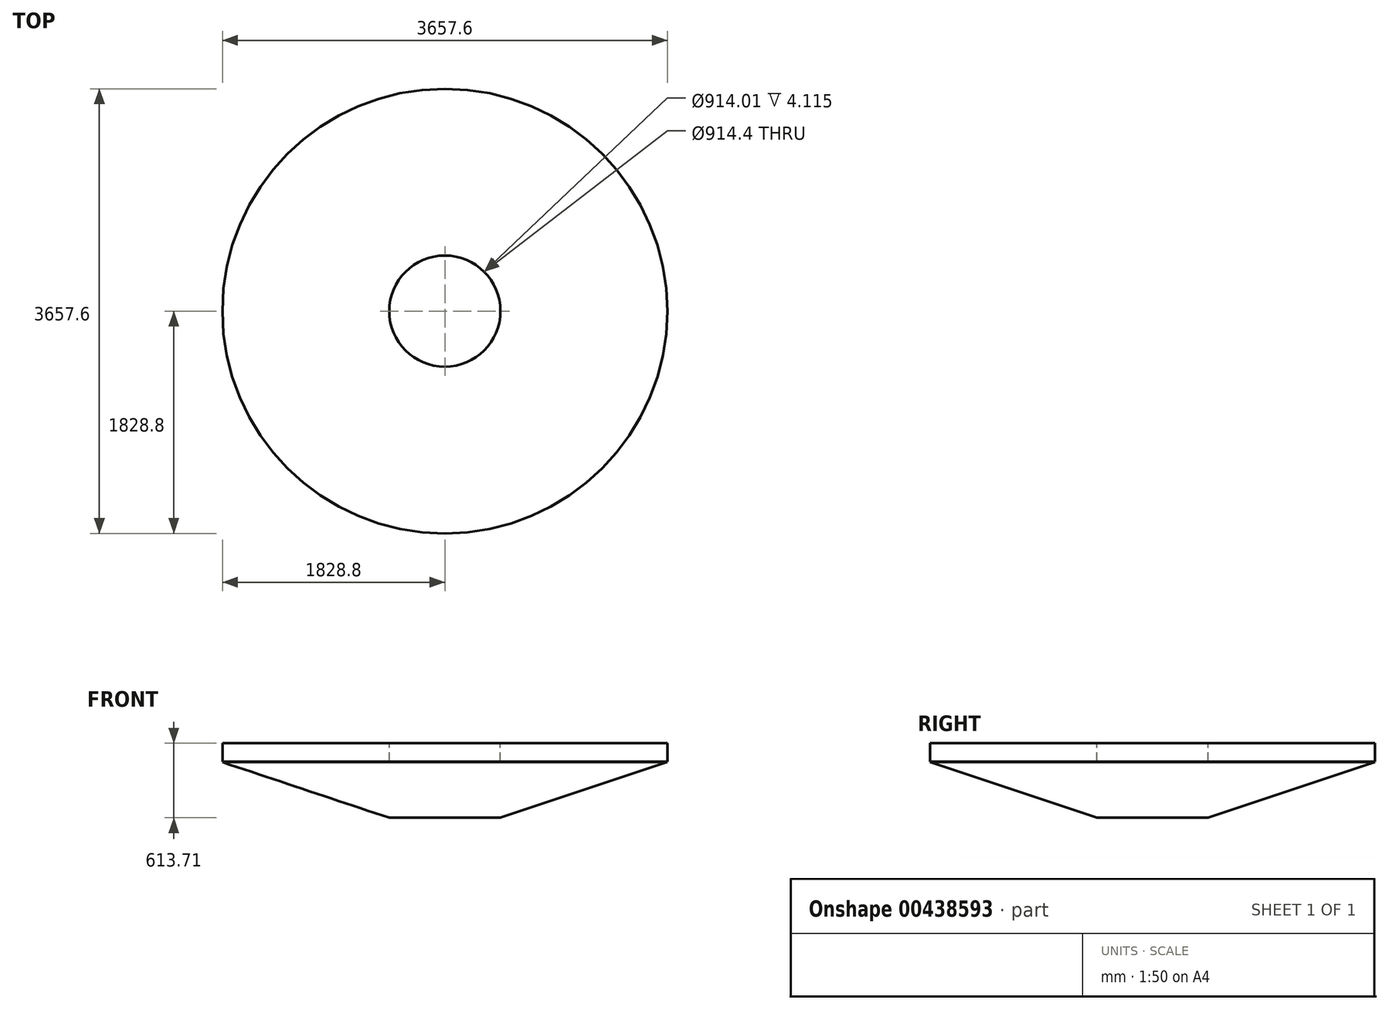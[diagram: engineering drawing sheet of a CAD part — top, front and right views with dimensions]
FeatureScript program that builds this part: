
annotation { "Feature Type Name" : "Feature", "Feature Type Description" : "" }
export const myFeature = defineFeature(function(context is Context, id is Id, definition is map)
    precondition{}
    {
        {
            var Q0;
            Q0=qCreatedBy(makeId("Top.planeOp"),FACE);
            var sketch = newSketch(context, id + "F0", { "sketchPlane" : qUnion([Q0])});
            skCircle(sketch, "E0", {"center": v(0, 0) * mm, "radius": 457.2 * mm});
            skCircle(sketch, "E1", {"center": v(0, 0) * mm, "radius": 1828.8 * mm});
            skSolve(sketch);
        }
        {
            var Q0;
            Q0=qCreatedBy(makeId("Top.planeOp"),FACE);
            var sketch = newSketch(context, id + "F1", { "sketchPlane" : qUnion([Q0])});
            skCircle(sketch, "E2", {"center": v(0, 0) * mm, "radius": 457.2 * mm});
            skSolve(sketch);
        }
        {
            var Q0;
            Q0 = qSketchRegion(id + "F1", true);
            extrude(context, id + "F2", {"entities" : qUnion([Q0]), "depth" : -609.6 * mm});
        }
        {
            var Q0;
            Q0=makeQuery(id+"F0.imprint","IMPRINT",FACE,{"disambiguationData":[TD([[makeQuery(id+"F0.imprint","IMPRINT",EDGE,{"derivedFrom":sQuery(id+"F0.wireOp",EDGE,"E0")}),-1.0]])]});
            extrude(context, id + "F3", {"entities" : qUnion([Q0]), "depth" : -152.4 * mm});
        }
        {
            var Q0;
            Q0=qCreatedBy(makeId("Front.planeOp"),FACE);
            var sketch = newSketch(context, id + "F4", { "sketchPlane" : qUnion([Q0])});
            skPoint(sketch, "E3", {"position": v(-457, -152.45) * mm});
            skPoint(sketch, "E4", {"position": v(-457, -613.71) * mm});
            skPoint(sketch, "E5", {"position": v(-1828.8, -152.45) * mm});
            skLineSegment(sketch, "E6", {"start": v(-1828.6, -156.51) * mm, "end": v(-457, -613.71) * mm});
            skLineSegment(sketch, "E7", {"start": v(-457, -156.51) * mm, "end": v(-457, -613.71) * mm});
            skLineSegment(sketch, "E8", {"start": v(-457, -156.51) * mm, "end": v(-1828.6, -156.51) * mm});
            skSolve(sketch);
        }
        {
            var Q0;
            Q0 = qSketchRegion(id + "F4", true);
            var Q1;
            Q1=makeQuery(id+"F2.opExtrude","CAP_EDGE",EDGE,{"disambiguationData":[OSD([sQuery(id+"F1.wireOp",EDGE,"E2")])],"isStart":false});
            revolve(context, id + "F5", {"operationType" : NewBodyOperationType.ADD, "entities" : qUnion([Q0]), "axis" : qUnion([Q1]), "revolveType" : RevolveType.FULL});
        }
    });
